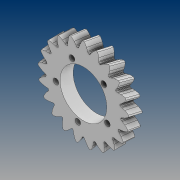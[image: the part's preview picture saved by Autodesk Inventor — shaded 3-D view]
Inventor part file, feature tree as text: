
AUTODESK INVENTOR PART (.ipt)
format: ipt  version: 2021 (Build 250183000, 183)  size: 799,744 bytes
history: native  units: mm
features: thread x5, extrude x2, sketch x1, pattern_circular x1
ambient origin geometry x8: Origin, YZ Plane, XZ Plane, XY Plane, X Axis, Y Axis, Z Axis, Center Point
bodies: Solid2 (feature_tree), Solid1 (feature_tree)
feature tree (9):
  sketch  "Sketch1"  dims[d0=100.0mm d1=0.0mm d2=0.0mm d3=59.0mm d4=90.0deg d5=12.0mm d6=0.0mm d7=0.0mm d8=50.0mm d9=360.0deg d11=27.996mm d12=0.0mm d13=27.996mm d14=0.0mm d15=27.996mm d16=0.0mm d17=27.996mm d18=0.0mm d19=27.996mm d20=0.0mm]
  extrude  "Extrusion1"  TaperAngle=0.0deg  [1 undecoded]
  extrude  "Extrusion2"  Depth=50.0mm
  pattern_circular  "Circular Pattern1"  Angle=90.0deg  [1 undecoded]
  thread  "Thread1"  [1 undecoded]
  thread  "Thread2"  [1 undecoded]
  thread  "Thread3"  [1 undecoded]
  thread  "Thread4"  [1 undecoded]
  thread  "Thread5"  [1 undecoded]
note: 7 required parameter values undecoded (feature->parameter linkage not recoverable at this tier; creation-order binding heuristic only, values carry confidence <= 0.55)
